# Revit family: PANZERI_GINEVRA_SUSPENSION_LIGHT
name_source: partatom
category: Lighting Fixtures
revit_build: Autodesk Revit 2018 (Build: 20190510_1515(x64)
units: mm (PartAtom-declared; Revit-internal decimal feet)

## family parameters
Cut with Voids When Loaded = No
Host = Face
Light Source = No
OmniClass Number = 23.80.70.00
OmniClass Title = Lighting
Part Type = Normal
Room Calculation Point = Yes
Round Connector Dimension = Use Diameter
Shared = No

## types (2) — shared parameters
ACCESSORIES = DRIVER: integrated included | Power canopy and covering inclued
AVAILABLE FINISHES = Structure: mat black and gold or white and gold; Canopy: white or mat black. CUSTOM finishes available only on request.
Apparent Load = 0 VA
BIM BADGE = https://bim.archiproducts.com
BODY AND LIGHT SOURCE = 1_Body_LightSource_PANZERI_GINEVRA_SUSPENSION_LIGHT : Ø53cm_3000K
CABLE MATERIAL = PANZERI_PVC_TRANSPARENT
CANOPY MATERIAL = PANZERI_ALUMINIUM_POLYACRYLIC_PAINT_MAT_BLACK_06
CANOPY_VISIBILITY = Yes
COLLECTION = GINEVRA
COLOR RENDERING INDEX = Ra>90
Default Elevation = 1219 mm
Description = Suspension lighting fixture for interiors, with direct and indirect light emission.
ENERGY EFFICIENCY CLASS = N/D
FREQUENCY = 0 Hz
FREQUENCY RANGE = 50/60Hz
INSTALLATION INSTRUCTIONS = https://panzeri.it
IP RATING = IP20
LAMP MATERIAL = PANZERI_POLYCARBONATE_OPALINE_SCREEN_Light_on
Lamp = LED
Light Source Symbol Size = 300 mm
MATERIAL DESCRIPTION = Pickled sheet metal cap in polyacrylic paint. Turned aluminium structure in polyacrylic paint. Pickled sheet metal wiring support plate in polyacrylic paint. Moulded polycarbonate micro-prismatic diffuser. 2m <78,7in> long steel suspension cables. 2,2m <86,6in> long power cable in transparent PVC.
Manufacturer = PANZERI
Model = GINEVRA SUSPENSION
POWER SUPPLY = 220-240V AC
PRODUCT SHEET = https://www.archiproducts.com
STRUCTURE MATERIAL = PANZERI_ALUMINIUM_POLYACRYLIC_PAINT_MAT_BLACK_06
TECHNICAL SHEET = https://panzeri.it
Type Comments = Direct and indirect light emission.
URL = https://panzeri.it
USAGE = INDOOR - SUSPENSION
VOLTAGE = 0 V

## per-type parameters (varying)
| type | DIAMETER | HEIGHT | LIGHTING SPECIFICATION | PACKAGING | PRODUCT CODE | WATTAGE | WEIGHT |
| Ø53cm_3000K_Black | 530 mm | 110 mm | LED 36W / 3000K / Ra>90 / 2916lm / 220-240V AC / dimmable (DALI/Push DIM) | 20,0 x 62,0 x 62,0 cm | L09280.050.0402 | 36 W | 6.27 kg |
| Ø80cm_3000K_Black | 800 mm | 140 mm | LED 82W / 3000K / Ra>90 / 7782lm / 220-240V AC / dimmable (DALI/Push DIM) | 18,0 x 90,0 x 90,0 cm | L09280.080.0402 | 82 W | 10.97 kg |

## geometry (parser evidence)
native form markers: Sweep x7
no freeform markers — native parametric forms only
